# Revit family: Storage-Freestanding-Teknion-BSMPS_Mid_Height_Stretch_Pedestal-R2018
name_source: partatom
category: Furniture
revit_build: Autodesk Revit 2018 (Build: 20190510_1515(x64)
units: mm (PartAtom-declared; Revit-internal decimal feet)

## family parameters
Always vertical = Yes
Cut with Voids When Loaded = No
OmniClass Number = 23.40.20.00
OmniClass Title = General Furniture and Specialties
Room Calculation Point = No
Shared = Yes
Work Plane-Based = No

## types (4) — shared parameters
Assembly Code = E2020200
Manufacturer = Teknion
Manufacturer Fax = 416.661.4586
Part Number = BSMPS
Product Documentation Link = https://www.teknion.com
Product Line = Expansion Casegoods
Product Page URL = https://www.teknion.com
Series = Expansion Casegoods
Sustainability Data = https://www.teknion.com
URL = www.teknion.com
Unit Weight URL = http://www.teknion.com
Warranty = http://www.teknion.com

## per-type parameters (varying)
| type | Description | Model | Width |
| 16" Width | Mid-Height Stretch Pedestal, 16" Width, 21" Height | BSMPS_1621 | 15.5 " |
| 24" Width | Mid-Height Stretch Pedestal, 24" Width, 21" Height | BSMPS_1624 | 23.88 " |
| 30" Width | Mid-Height Stretch Pedestal, 30" Width, 21" Height | BSMPS_1630 | 29.85 " |
| 36" Width | Mid-Height Stretch Pedestal, 36" Width, 21" Height | BSMPS_1636 | 35.82 " |

## geometry (parser evidence)
native form markers: Sweep x1
no freeform markers — native parametric forms only
